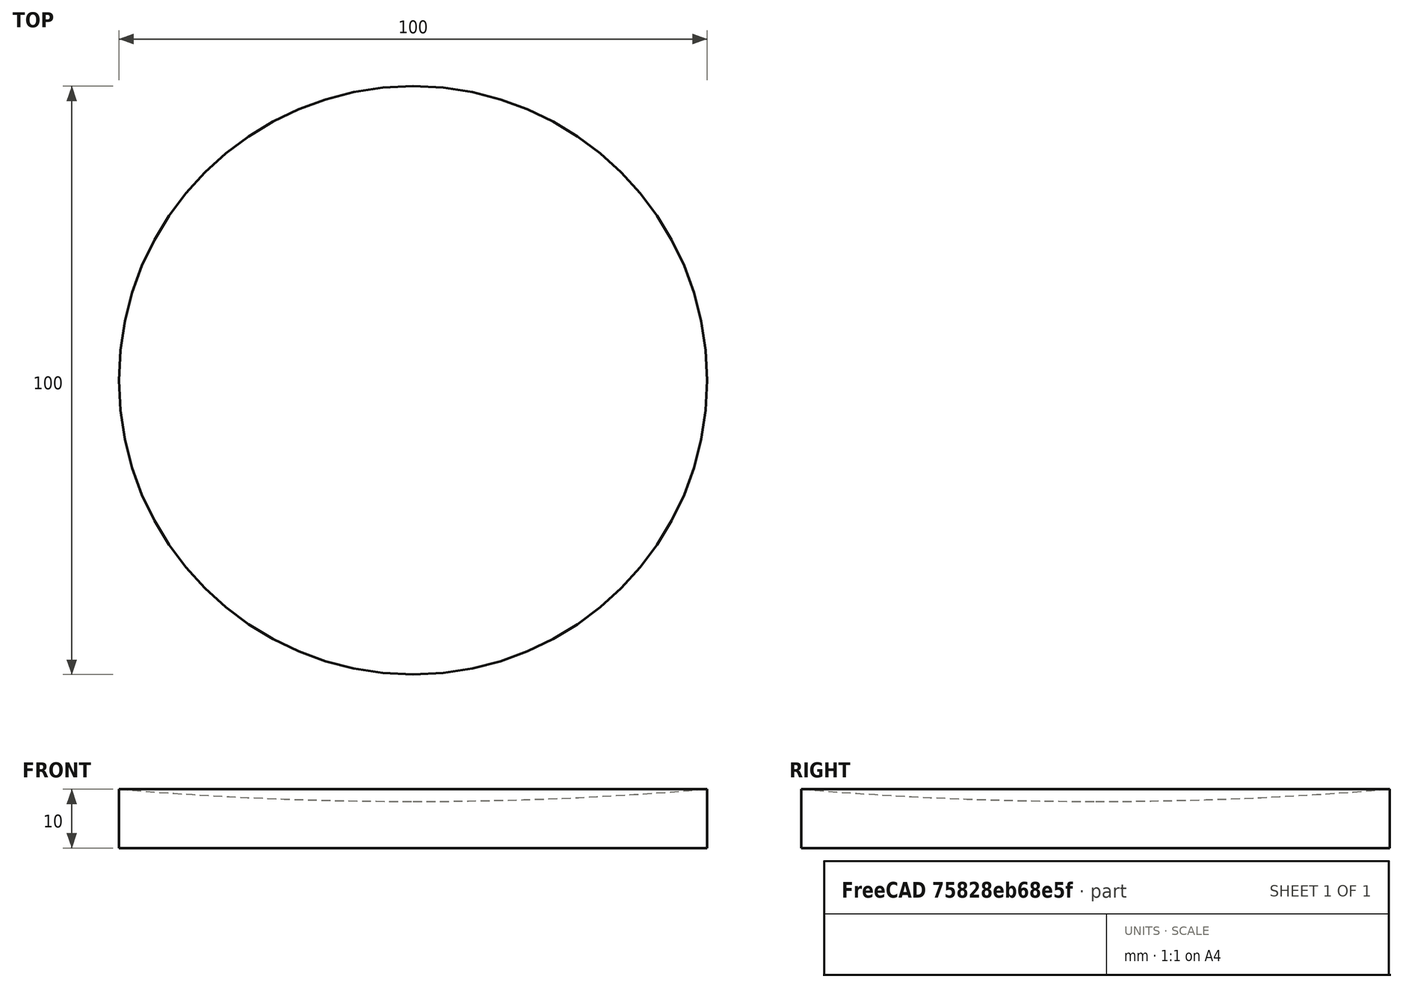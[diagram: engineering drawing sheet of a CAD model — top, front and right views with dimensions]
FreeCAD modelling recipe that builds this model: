
FCSTD DOCUMENT  (FreeCAD 0.21R33668 +7 (Git))
Label: ConcaveMirror
License: All rights reserved
LicenseURL: https://en.wikipedia.org/wiki/All_rights_reserved
objects: Part::Cylinder×2, Part::Sphere×2, Part::Cut×2, Part::FeaturePython×2, Spreadsheet::Sheet×1
note: 8 computed .brp shape members not serialized (recipe doc carries the construction recipe); baked Part::Feature solids carry a one-line shape summary decoded from their .brp

FEATURE [Spreadsheet::Sheet] Spreadsheet  label="ConcaveMirrorConfig"
  cells = A2='Diameter; B2(dia)=100; C2='Mirror diameter; E2='Radius of curvature; F2(curvature_r)==2 * f / cos(angle_inc); A3='Focal length; B3(f)=300; C3='Focal length of the mirror (tangential); E3='Sagital focal length; F3(f_sagital)==curvature_r / 2 / cos(angle_inc); A4='Incidence angle; B4(angle_inc)=0; E4='Thinnest region; F4(thinnest_region)==thickness - (curvature_r - sqrt(curvature_r * curvature_r - dia / 2 * dia / 2)); G4='Has to stay positive!; A5='Substrate thickness; B5(thickness)=10
FEATURE [Part::Cylinder] Cylinder
  Angle = 360
  AttacherType = Attacher::AttachEngine3D
  FirstAngle = 0
  Height = 10
  Radius = 50
  SecondAngle = 0
  expr: Height = <<ConcaveMirrorConfig>>.thickness
  expr: Radius = <<ConcaveMirrorConfig>>.dia / 2
FEATURE [Part::Sphere] Sphere
  Angle1 = -90
  Angle2 = 90
  Angle3 = 360
  AttacherType = Attacher::AttachEngine3D
  Placement = pos=(0,0,607.913) rot=(0,0,1;0rad)
  Radius = 600
  expr: .Placement.Base.z = <<ConcaveMirrorConfig>>.curvature_r + <<ConcaveMirrorConfig>>.thinnest_region
  expr: Radius = <<ConcaveMirrorConfig>>.curvature_r
FEATURE [Part::Cut] Cut
  Base = -> Cylinder
  Tool = -> Sphere
FEATURE [Part::FeaturePython] Beam  # WARN: FeaturePython — macro-defined, semantics opaque (R4)
  BeamDistance = 5
  BeamNrColumns = 10
  BeamNrRows = 10
  ConeAngle = 360
  HideFirstPart = true
  MaxNrReflections = 200
  MaxRayLength = 1000000
  Placement = pos=(-25,-25,600) rot=(0,1,0;1.5708rad)
  Power = true
  Spherical = false
  Wavelength = 580
  expr: .Placement.Base.z = 2 * <<ConcaveMirrorConfig>>.f
FEATURE [Part::FeaturePython] Mirror  # WARN: FeaturePython — macro-defined, semantics opaque (R4)
  Base = -> [Cut]
  HitsFromBeam = 100
  OpticalType = 0
FEATURE [Part::Cylinder] Cylinder001
  Angle = 360
  AttacherType = Attacher::AttachEngine3D
  FirstAngle = 0
  Height = 10
  Radius = 50
  SecondAngle = 0
  expr: Height = <<ConcaveMirrorConfig>>.thickness
  expr: Radius = <<ConcaveMirrorConfig>>.dia / 2
FEATURE [Part::Sphere] Sphere001
  Angle1 = -90
  Angle2 = 90
  Angle3 = 360
  AttacherType = Attacher::AttachEngine3D
  Placement = pos=(0,0,607.913) rot=(0,0,1;0rad)
  Radius = 600
  expr: .Placement.Base.z = <<ConcaveMirrorConfig>>.curvature_r + <<ConcaveMirrorConfig>>.thinnest_region
  expr: Radius = <<ConcaveMirrorConfig>>.curvature_r
FEATURE [Part::Cut] Cut001  label="ConcaveMirror"
  Base = -> Cylinder001
  Tool = -> Sphere001
